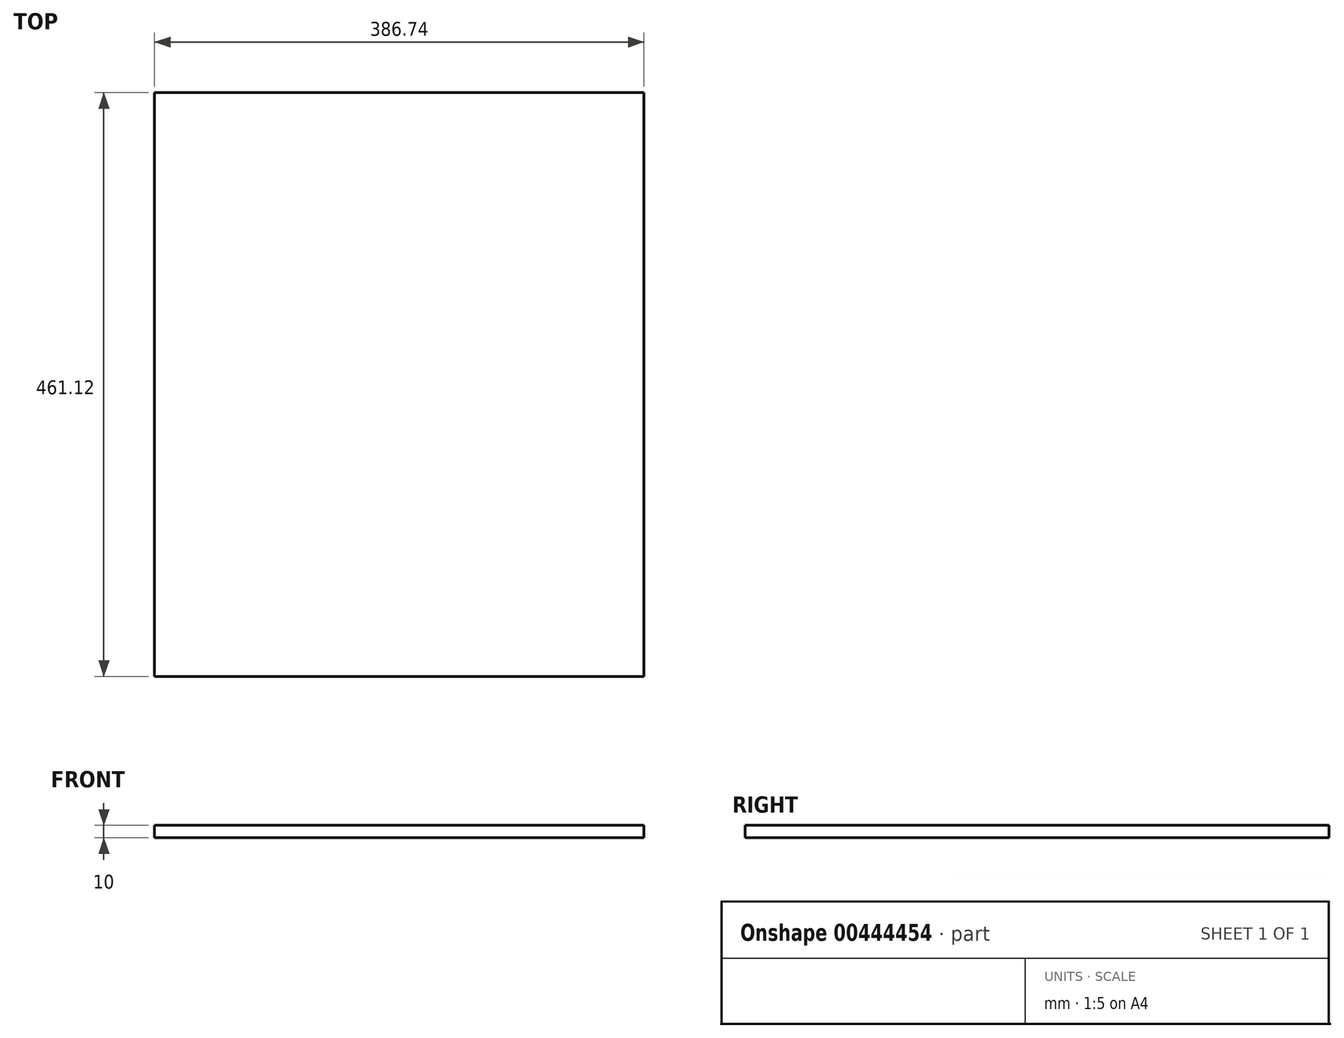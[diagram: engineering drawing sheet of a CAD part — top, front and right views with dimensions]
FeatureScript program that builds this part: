
annotation { "Feature Type Name" : "Feature", "Feature Type Description" : "" }
export const myFeature = defineFeature(function(context is Context, id is Id, definition is map)
    precondition{}
    {
        {
            var Q0;
            Q0=qCreatedBy(makeId("Top.planeOp"),FACE);
            var sketch = newSketch(context, id + "F0", { "sketchPlane" : qUnion([Q0])});
            skLineSegment(sketch, "E0.bottom", {"start": v(193.37, 230.56) * mm, "end": v(-193.37, 230.56) * mm});
            skLineSegment(sketch, "E0.top", {"start": v(193.37, -230.56) * mm, "end": v(-193.37, -230.56) * mm});
            skLineSegment(sketch, "E0.left", {"start": v(193.37, 230.56) * mm, "end": v(193.37, -230.56) * mm});
            skLineSegment(sketch, "E0.right", {"start": v(-193.37, 230.56) * mm, "end": v(-193.37, -230.56) * mm});
            skPoint(sketch, "E0.middle", {"position": v(0, 0) * mm});
            skLineSegment(sketch, "E1", {"start": v(0, 0) * mm, "end": v(0, 288.24) * mm, "construction": true});
            skLineSegment(sketch, "E2", {"start": v(0, 0) * mm, "end": v(0, -323.53) * mm, "construction": true});
            skLineSegment(sketch, "E3", {"start": v(0, 230.56) * mm, "end": v(36.97, 160.08) * mm});
            skLineSegment(sketch, "E4", {"start": v(56.98, 90.97) * mm, "end": v(58.5, 72.2) * mm});
            skLineSegment(sketch, "E5", {"start": v(58.5, 72.2) * mm, "end": v(72.99, 73.37) * mm});
            skLineSegment(sketch, "E6", {"start": v(160.6, 80.45) * mm, "end": v(88.88, 0) * mm});
            skLineSegment(sketch, "E7", {"start": v(88.88, 0) * mm, "end": v(183.42, -116.45) * mm});
            skLineSegment(sketch, "E8", {"start": v(183.42, -116.45) * mm, "end": v(0, -83.45) * mm});
            skLineSegment(sketch, "E9", {"start": v(0, 124.04) * mm, "end": v(0, -83.45) * mm});
            skLineSegment(sketch, "E10.trimOffspring", {"start": v(114.8, 76.74) * mm, "end": v(160.6, 80.45) * mm});
            skArc(sketch, "E11.filletArc", {"start": v(56.98, 90.97) * mm, "mid": v(50.46, 126.53) * mm, "end": v(36.97, 160.08) * mm});
            skPoint(sketch, "E12", {"position": v(115.01, 87.92) * mm});
            skLineSegment(sketch, "E13", {"start": v(72.99, 73.37) * mm, "end": v(115.01, 87.92) * mm});
            skArc(sketch, "E14", {"start": v(114.8, 76.74) * mm, "mid": v(113.01, 82.23) * mm, "end": v(114.58, 87.77) * mm});
            skSolve(sketch);
        }
        {
            var Q0;
            Q0=makeQuery(id+"F0.imprint","IMPRINT",FACE,{"disambiguationData":[TD([[makeQuery(id+"F0.imprint","IMPRINT",EDGE,{"derivedFrom":sQuery(id+"F0.wireOp",EDGE,"E0.bottom")}),1.0]])]});
            extrude(context, id + "F1", {"entities" : qUnion([Q0]), "depth" : 10 * mm});
        }
    });
